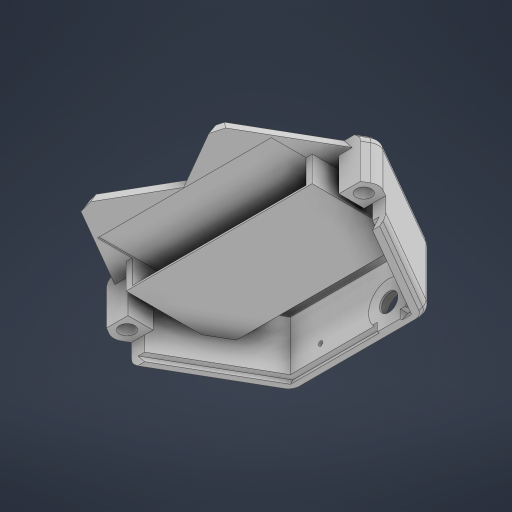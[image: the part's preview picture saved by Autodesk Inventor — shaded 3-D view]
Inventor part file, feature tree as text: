
AUTODESK INVENTOR PART (.ipt)
format: ipt  version: 2023 (Build 270158000, 158)  size: 950,784 bytes
history: native  units: in
note: dims shown in document units (in); Inventor stores cm internally (conversion verified against a paired STEP export)
features: extrude x27, sketch x17, move_body x14, direct_edit x9, draft x6, plane x3, fillet x3, chamfer x3, other x1
ambient origin geometry x8: Origin, YZ Plane, XZ Plane, XY Plane, X Axis, Y Axis, Z Axis, Center Point
bodies: Solid1 (feature_tree)
feature tree (83):
  sketch  "Sketch1"  dims[d0=1.939in d1=0.5118in d2=0.374in d3=0.4449in d4=0.0295in d5=0.0728in d6=0.1378in d7=0.0787in d8=0.0in d9=0.6181in d10=0.0in]
  extrude  "Extrusion1"  Depth=0.0787in TaperAngle=0.0deg
  extrude  "Extrusion2"  Depth=0.0906in
  extrude  "Extrusion3"  Depth=0.2205in TaperAngle=0.0deg
  sketch  "Sketch4"  dims[d15=0.0in d16=0.0in d17=0.2205in d18=0.0in]
  extrude  "Extrusion4"  Depth=1.5748in
  extrude  "Extrusion5"  Depth=0.0394in
  extrude  "Extrusion6"  Depth=0.2283in TaperAngle=0.0deg
  extrude  "Extrusion7"  Depth=0.0787in TaperAngle=0.0deg
  extrude  "Extrusion8"  Depth=0.3937in
  plane  "Work Plane1"
  extrude  "Extrusion9"  Depth=0.3937in TaperAngle=0.0deg
  extrude  "Extrusion10"  Depth=0.3937in TaperAngle=0.0deg
  plane  "Work Plane2"
  sketch  "Sketch7"  dims[d19=0.4764in d20=0.0in d21=1.5748in]
  extrude  "Extrusion11"  Depth=0.0787in TaperAngle=0.0deg
  extrude  "Extrusion12"  Depth=0.0787in
  extrude  "Extrusion14"  Depth=0.2405in
  extrude  "Extrusion15"  Depth=0.3937in TaperAngle=0.0deg
  direct_edit  "Direct Edit5"
  plane  "Work Plane3"
  sketch  "Sketch11"  dims[d32=0.0787in d33=0.0591in d34=0.0in]
  extrude  "Extrusion16"  Depth=0.3937in
  extrude  "Extrusion17"  [1 undecoded]
  draft  "FaceDraft1"
  draft  "FaceDraft2"
  draft  "FaceDraft3"
  extrude  "Extrusion18"  Depth=0.0787in TaperAngle=0.0deg
  draft  "FaceDraft5"
  direct_edit  "Direct Edit6"
  sketch  "Sketch12"  dims[d35=0.3937in d36=0.0in d38=0.2405in]
  sketch  "Sketch13"  dims[d40=0.0787in d41=0.3937in d42=0.0in]
  fillet  "Fillet1"  [1 undecoded]
  fillet  "Fillet2"  Radius=0.2405in
  chamfer  "Chamfer2"  Angle=90.0deg  [1 undecoded]
  fillet  "Fillet3"  Radius=0.2405in
  extrude  "Extrusion19"  Depth=0.0787in TaperAngle=0.0deg
  extrude  "Extrusion20"  Depth=0.0787in
  sketch  "Sketch15"  dims[d61=0.0689in d62=0.0in d72=0.0in d73=0.0in d74=0.0787in]
  sketch  "Sketch16"  dims[d75=0.0in d76=0.0in d77=0.0787in d81=0.0591in]
  extrude  "Extrusion22"  Depth=0.0787in
  extrude  "Extrusion23"  Depth=0.0787in
  direct_edit  "Direct Edit7"
  extrude  "Extrusion24"  Depth=0.0787in TaperAngle=45.0deg
  extrude  "Extrusion25"  Depth=0.0787in
  extrude  "Extrusion26"  Depth=0.0787in TaperAngle=0.0deg
  chamfer  "Chamfer3"  Distance=0.2008in
  extrude  "Extrusion27"  Depth=0.0787in
  draft  "FaceDraft6"
  draft  "FaceDraft7"
  direct_edit  "Direct Edit9"
  direct_edit  "Direct Edit10"
  extrude  "Extrusion28"  Depth=0.0787in
  direct_edit  "Direct Edit11"
  direct_edit  "Direct Edit12"
  direct_edit  "Direct Edit13"
  extrude  "Extrusion29"  TaperAngle=0.0deg  [1 undecoded]
  chamfer  "Chamfer4"  Distance=0.2953in
  direct_edit  "Direct Edit14"
  sketch  "Sketch3"  dims[d11=0.5906in d12=0.0in d14=0.0906in]
  sketch  "Sketch9"  dims[d22=1.1811in d23=0.0394in]
  sketch  "Sketch10"  dims[d24=0.2441in d25=0.0in d26=0.2283in d27=0.0in]
  other  "Image1"
  sketch  "Sketch14"  dims[d43=0.3937in d44=0.0in d59=0.0689in d60=0.0in]
  sketch  "Sketch17"  dims[d82=90.0deg d83=0.2405in]
  sketch  "Sketch18"  dims[d84=0.0787in d85=0.3937in d86=0.0in]
  sketch  "Sketch19"  dims[d87=0.3937in d88=0.0in d89=0.2405in]
  sketch  "Sketch20"  dims[d90=-0.2061in d91=-0.2061in]
  sketch  "Sketch21"  dims[d93=0.5118in d94=0.0118in d95=0.0in d96=90.0deg d97=0.2405in d98=90.0deg d99=0.2405in d100=0.0in d101=0.0in d102=0.0157in d111=0.1969in d113=2.4409in d115=1.939in d116=0.5118in d117=0.374in d118=0.4134in d119=0.0295in d120=0.0728in d121=0.1378in d122=0.1181in d124=0.1575in d125=0.0492in d126=0.0787in d127=45.0deg d128=0.0787in d186=0.0236in d187=0.0in d188=0.2008in d189=0.1102in d190=0.1732in d191=0.0in d192=0.0in d193=0.2953in d196=0.7744in d197=0.1024in d198=0.0394in d199=0.0in d200=0.0in d201=0.2165in d202=0.3937in d203=0.0in d204=0.0in d205=0.0in d206=-0.4375in d207=0.1181in d208=0.0in d222=0.6871in d223=0.0in d224=0.0in d225=0.0118in d226=0.0in d227=0.0394in d228=0.0118in d229=45.0deg d234=45.0deg d235=0.3937in d236=0.0in d237=-0.2061in d238=-0.2061in d239=0.0in d240=0.0in d241=0.0091in d242=0.0in d243=0.0in d244=0.0091in d245=0.0in d246=0.0in d247=-0.0118in d248=0.0in d249=0.0in d250=-0.0118in d255=0.0394in d256=0.0in d257=0.0in d258=0.0in d259=-0.0098in d264=0.0in d265=0.0in d266=0.0591in d267=0.0in d268=0.0in d269=0.0591in d270=0.1496in d271=0.1417in d273=0.0in d274=0.0in d275=-0.0197in d276=0.0in d277=0.0in d278=0.0197in d280=0.1417in d281=0.1535in d282=0.0079in d283=0.0079in d286=0.1181in d287=0.4331in d288=0.1181in d289=0.0591in d290=0.0in d291=0.0591in d292=0.0787in d293=45.0deg d294=0.0073in d296=0.0in d297=0.0in d298=-0.0118in d45=0.0197in d46=0.0344in d47=0.0197in d48=0.0344in d103=0.0344in]
  move_body  "Move8"
  move_body  "Move9"
  move_body  "Move10"
  move_body  "Move11"
  move_body  "Move16"
  move_body  "Move17"
  move_body  "Move18"
  move_body  "Move19"
  move_body  "Move20"
  move_body  "Move21"
  move_body  "Move22"
  move_body  "Move23"
  move_body  "Move24"
  move_body  "Move25"
note: 4 required parameter values undecoded (feature->parameter linkage not recoverable at this tier; creation-order binding heuristic only, values carry confidence <= 0.55)
